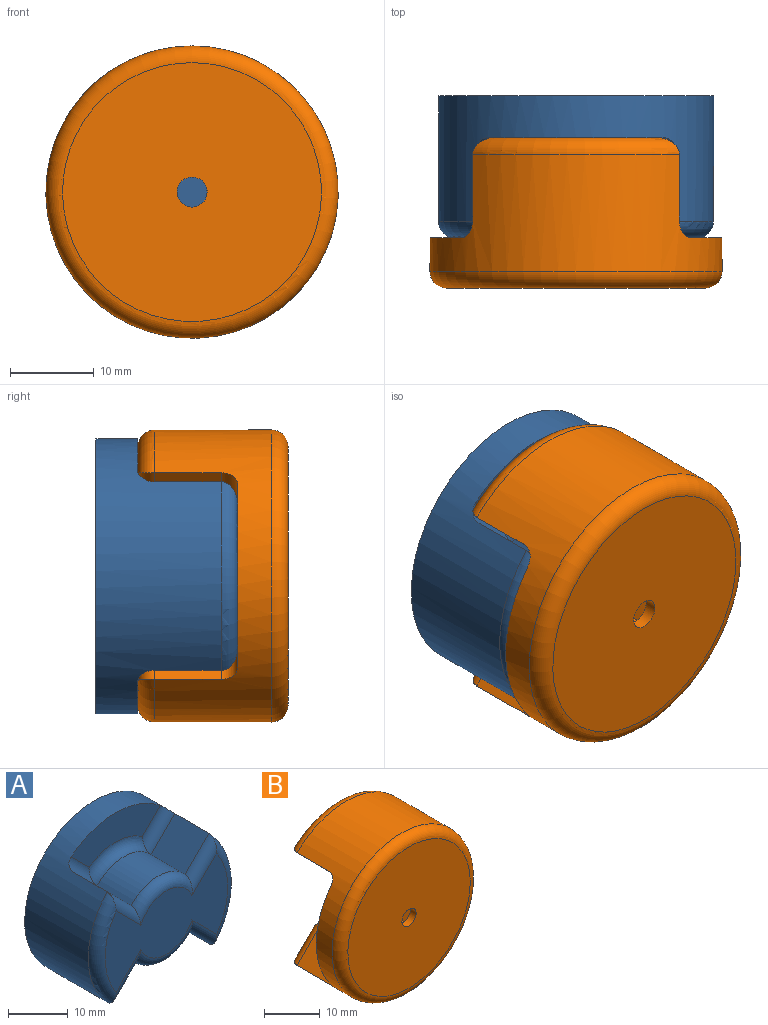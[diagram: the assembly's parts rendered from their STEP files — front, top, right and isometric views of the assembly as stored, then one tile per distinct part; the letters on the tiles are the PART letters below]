
ASSEMBLY  parts=2 mates=1
PART A: 36 faces, bbox 35.7x17x33 mm
  f0: plane 32.95x32.95mm, normal (0,1,0), area 678.7mm2, adj f7,f11,f12,f13,f14,f30,f31,f32
  f1: plane 8x5.65mm, normal (0.71,0,0.71), area 63.9mm2, adj f6,f7,f21,f25
  f2: plane 8x5.65mm, normal (0.71,0,-0.71), area 63.9mm2, adj f3,f7,f18,f22
  f3: cylinder r=8.5mm len=12.71mm, axis (0,1,0), area 114.8mm2, adj f2,f4,f17,f24
  f4: plane 8x5.65mm, normal (-0.71,0,-0.71), area 63.9mm2, adj f3,f7,f16,f26
  f5: plane 8x5.65mm, normal (-0.71,0,0.71), area 63.9mm2, adj f6,f7,f19,f29
  f6: cylinder r=8.5mm len=12.71mm, axis (0,1,0), area 114.8mm2, adj f1,f5,f20,f27
  f7: cylinder r=16.48mm len=32.95mm, axis (0,1,0), area 1018.7mm2, adj f0,f1,f2,f4,f5,f9,f10,f16
  f8: plane 28.95x16.63mm, normal (0,-1,0), area 314.9mm2, adj f22,f23,f24,f25,f26,f27,f28,f29
  f9: plane 21.08x8.07mm, normal (0,-1,0), area 108.7mm2, adj f7,f19,f20,f21
  f10: plane 21.08x8.07mm, normal (0,-1,0), area 108.7mm2, adj f7,f16,f17,f18
  f11: plane 9.5x4.5mm, normal (1,0,0), area 42.7mm2, adj f0,f15,f32,f33
  f12: plane 9.5x4.5mm, normal (0,0,-1), area 42.7mm2, adj f0,f15,f31,f32
  f13: plane 9.5x4.5mm, normal (-1,0,0), area 42.7mm2, adj f0,f15,f30,f31
  f14: plane 9.5x4.5mm, normal (0,0,1), area 42.7mm2, adj f0,f15,f30,f33
  f15: plane 13.5x13.5mm, normal (0,1,0), area 154.6mm2, adj f11,f12,f13,f14,f30,f31,f32,f33
  f16: cylinder r=2mm len=7.06mm, axis (0.71,0,-0.71), area 22.7mm2, adj f4,f7,f10,f17
  f17: torus R=10.5mm, axis (0,1,0), area 44.1mm2, adj f3,f10,f16,f18
  f18: cylinder r=2mm len=7.06mm, axis (0.71,0,0.71), area 22.7mm2, adj f2,f7,f10,f17
  f19: cylinder r=2mm len=7.06mm, axis (-0.71,0,-0.71), area 22.7mm2, adj f5,f7,f9,f20
  f20: torus R=10.5mm, axis (0,1,0), area 44.1mm2, adj f6,f9,f19,f21
  f21: cylinder r=2mm len=7.06mm, axis (-0.71,0,0.71), area 22.7mm2, adj f1,f7,f9,f20
  f22: cylinder r=2mm len=8.82mm, axis (-0.71,0,-0.71), area 25.3mm2, adj f2,f8,f23,f24
  f23: torus R=14.48mm, axis (0,-1,0), area 70mm2, adj f7,f8,f22,f25
  f24: torus R=6.5mm, axis (0,-1,0), area 46.1mm2, adj f3,f8,f22,f26
  f25: cylinder r=2mm len=8.82mm, axis (0.71,0,-0.71), area 25.3mm2, adj f1,f8,f23,f27
  f26: cylinder r=2mm len=8.82mm, axis (-0.71,0,0.71), area 25.3mm2, adj f4,f8,f24,f28
  f27: torus R=6.5mm, axis (0,-1,0), area 46.1mm2, adj f6,f8,f25,f29
  f28: torus R=14.48mm, axis (0,-1,0), area 70mm2, adj f7,f8,f26,f29
  f29: cylinder r=2mm len=8.82mm, axis (0.71,0,0.71), area 25.3mm2, adj f5,f8,f27,f28
  f30: plane 4.5x2mm, normal (-0.71,0,0.71), area 12.7mm2, adj f0,f13,f14,f15
  f31: plane 4.5x2mm, normal (-0.71,0,-0.71), area 12.7mm2, adj f0,f12,f13,f15
  f32: plane 4.5x2mm, normal (0.71,0,-0.71), area 12.7mm2, adj f0,f11,f12,f15
  f33: plane 4.5x2mm, normal (0.71,0,0.71), area 12.7mm2, adj f0,f11,f14,f15
  f34: cylinder r=2.5mm len=5mm, axis (0,1,0), area 31.4mm2, adj f15,f35
  f35: plane 5x5mm, normal (0,1,0), area 19.6mm2, adj f34
PART B: 32 faces, bbox 37.9x18x37.9 mm
  f0: cylinder r=1.8mm len=3.6mm, axis (0,-1,0), area 17mm2, adj f11,f12
  f1: plane 18.91x6.44mm, normal (0,1,0), area 75.6mm2, adj f19,f20,f21,f22
  f2: cylinder r=17.5mm len=35mm, axis (0,1,0), area 993mm2, adj f4,f6,f7,f9,f10,f22,f25,f27
  f3: plane 18.91x6.44mm, normal (0,1,0), area 75.6mm2, adj f23,f24,f25,f26
  f4: plane 8x6.01mm, normal (0.71,0,0.71), area 68mm2, adj f2,f5,f21,f28
  f5: cylinder r=9mm len=15.24mm, axis (0,1,0), area 143.1mm2, adj f4,f6,f10,f19,f27,f28
  f6: plane 8x6.01mm, normal (-0.71,0,0.71), area 68mm2, adj f2,f5,f20,f27
  f7: plane 8x6.01mm, normal (-0.71,0,-0.71), area 68mm2, adj f2,f8,f26,f29
  f8: cylinder r=9mm len=15.24mm, axis (0,1,0), area 143.1mm2, adj f7,f9,f10,f24,f29,f30
  f9: plane 8x6.01mm, normal (0.71,0,-0.71), area 68mm2, adj f2,f8,f23,f30
  f10: plane 35x21.76mm, normal (0,1,0), area 495.1mm2, adj f2,f5,f8,f13,f14,f15,f16,f17
  f11: plane 31x31mm, normal (0,-1,0), area 744.6mm2, adj f0,f31
  f12: plane 8.31x7.2mm, normal (0,1,0), area 34.7mm2, adj f0,f13,f14,f15,f16,f17,f18
  f13: plane 4.5x4.16mm, normal (0,0,-1), area 18.7mm2, adj f10,f12,f14,f18
  f14: plane 4.5x3.6mm, normal (-0.87,0,-0.5), area 18.7mm2, adj f10,f12,f13,f15
  f15: plane 4.5x3.6mm, normal (-0.87,0,0.5), area 18.7mm2, adj f10,f12,f14,f16
  f16: plane 4.5x4.16mm, normal (0,0,1), area 18.7mm2, adj f10,f12,f15,f17
  f17: plane 4.5x3.6mm, normal (0.87,0,0.5), area 18.7mm2, adj f10,f12,f16,f18
  f18: plane 4.5x3.6mm, normal (0.87,0,-0.5), area 18.7mm2, adj f10,f12,f13,f17
  f19: torus R=11mm, axis (0,-1,0), area 43.4mm2, adj f1,f5,f20,f21
  f20: cylinder r=2mm len=7.42mm, axis (-0.71,0,-0.71), area 22.2mm2, adj f1,f6,f19,f22
  f21: cylinder r=2mm len=7.42mm, axis (-0.71,0,0.71), area 22.2mm2, adj f1,f4,f19,f22
  f22: torus R=15.5mm, axis (0,-1,0), area 78.2mm2, adj f1,f2,f20,f21
  f23: cylinder r=2mm len=7.42mm, axis (0.71,0,0.71), area 22.2mm2, adj f3,f9,f24,f25
  f24: torus R=11mm, axis (0,-1,0), area 43.4mm2, adj f3,f8,f23,f26
  f25: torus R=15.5mm, axis (0,-1,0), area 78.2mm2, adj f2,f3,f23,f26
  f26: cylinder r=2mm len=7.42mm, axis (0.71,0,-0.71), area 22.2mm2, adj f3,f7,f24,f25
  f27: cylinder r=2mm len=7.58mm, axis (-0.71,0,-0.71), area 26.8mm2, adj f2,f5,f6,f10
  f28: cylinder r=2mm len=7.58mm, axis (-0.71,0,0.71), area 26.8mm2, adj f2,f4,f5,f10
  f29: cylinder r=2mm len=7.58mm, axis (0.71,0,-0.71), area 26.8mm2, adj f2,f7,f8,f10
  f30: cylinder r=2mm len=7.58mm, axis (0.71,0,0.71), area 26.8mm2, adj f2,f8,f9,f10
  f31: torus R=15.5mm, axis (0,-1,0), area 331.1mm2, adj f2,f11
PLACE A t=(10.86,6.27,-12.89)mm
PLACE B rot(axis=(0,1,0),180deg) t=(10.86,1.27,-12.89)mm
MATE fastened B.f2 <-> A.f7  axis (0,1,0) through (10.86,-10.73,-12.89)mm
